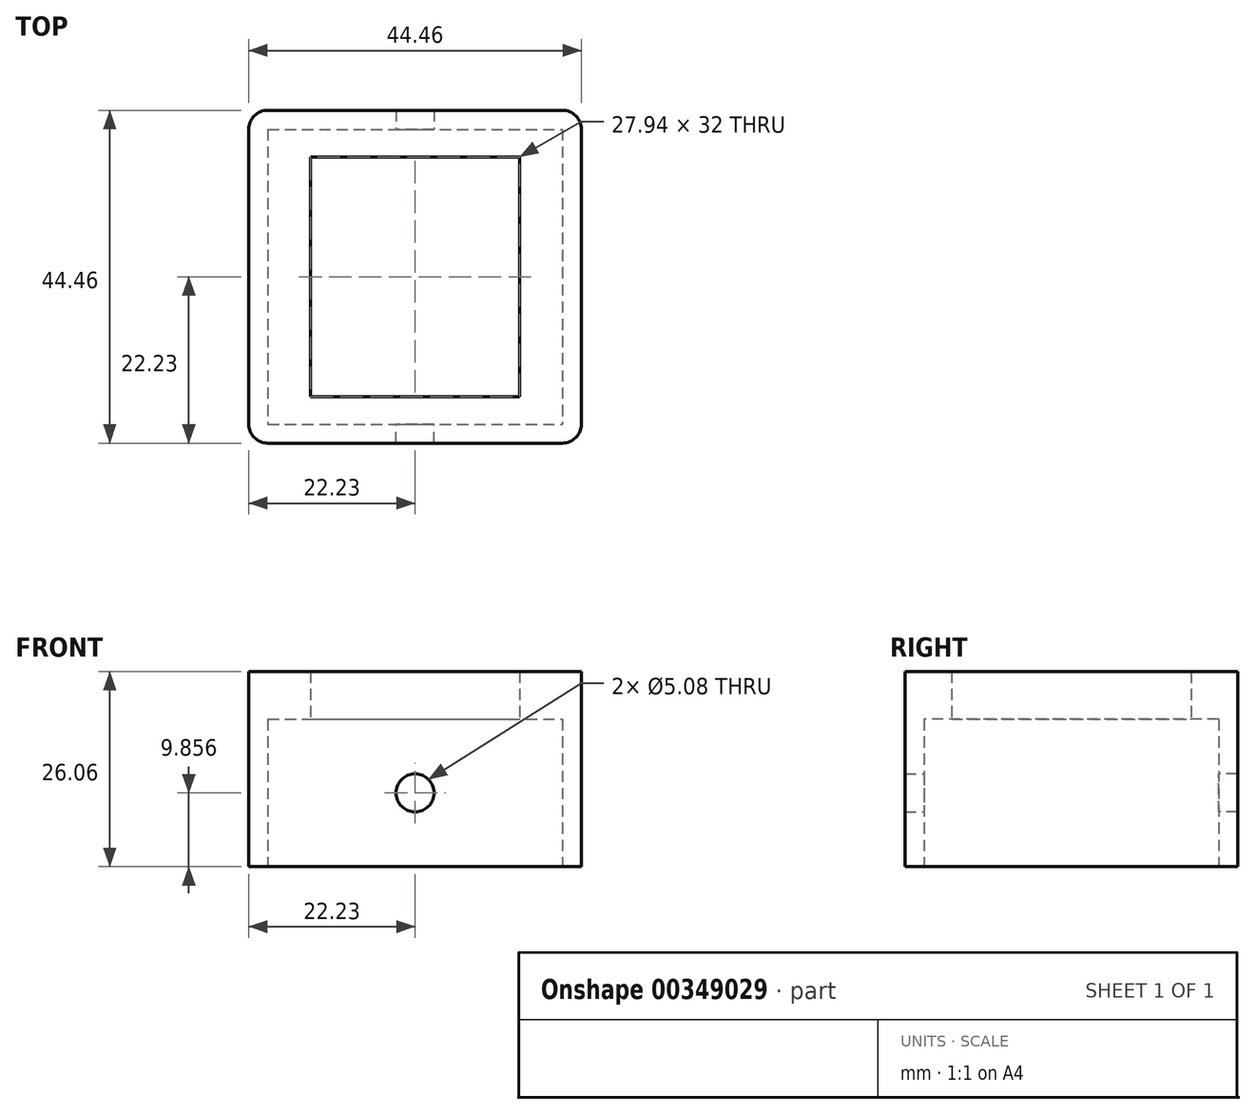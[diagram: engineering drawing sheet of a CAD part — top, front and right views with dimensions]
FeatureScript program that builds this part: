
annotation { "Feature Type Name" : "Feature", "Feature Type Description" : "" }
export const myFeature = defineFeature(function(context is Context, id is Id, definition is map)
    precondition{}
    {
        {
            var Q0;
            Q0=qCreatedBy(makeId("Top.planeOp"),FACE);
            var sketch = newSketch(context, id + "F0", { "sketchPlane" : qUnion([Q0])});
            skLineSegment(sketch, "E0.bottom", {"start": v(19.68, 19.69) * mm, "end": v(-19.69, 19.69) * mm});
            skLineSegment(sketch, "E0.top", {"start": v(19.69, -19.69) * mm, "end": v(-19.68, -19.69) * mm});
            skLineSegment(sketch, "E0.left", {"start": v(19.68, 19.69) * mm, "end": v(19.69, -19.69) * mm});
            skLineSegment(sketch, "E0.right", {"start": v(-19.69, 19.69) * mm, "end": v(-19.68, -19.69) * mm});
            skPoint(sketch, "E0.middle", {"position": v(0, 0) * mm});
            skLineSegment(sketch, "E1.0", {"start": v(19.69, -22.23) * mm, "end": v(-19.68, -22.23) * mm});
            skLineSegment(sketch, "E2.0", {"start": v(22.23, 19.69) * mm, "end": v(22.23, -19.69) * mm});
            skLineSegment(sketch, "E3.0", {"start": v(-22.23, 19.69) * mm, "end": v(-22.22, -19.69) * mm});
            skLineSegment(sketch, "E4.0", {"start": v(19.68, 22.23) * mm, "end": v(-19.69, 22.23) * mm});
            skArc(sketch, "E5", {"start": v(-19.69, 22.23) * mm, "mid": v(-20.82, 21.96) * mm, "end": v(-21.72, 21.21) * mm});
            skArc(sketch, "E6", {"start": v(-22.23, 19.69) * mm, "mid": v(-21.93, 20.86) * mm, "end": v(-21.13, 21.77) * mm});
            skArc(sketch, "E7", {"start": v(22.22, 19.69) * mm, "mid": v(21.48, 21.48) * mm, "end": v(19.68, 22.23) * mm});
            skArc(sketch, "E8", {"start": v(19.69, -22.23) * mm, "mid": v(21.48, -21.48) * mm, "end": v(22.23, -19.69) * mm});
            skArc(sketch, "E9", {"start": v(-22.22, -19.69) * mm, "mid": v(-21.48, -21.48) * mm, "end": v(-19.68, -22.23) * mm});
            skSolve(sketch);
        }
        {
            var Q0;
            Q0=qSketchRegion(id+"F0",true);
            extrude(context, id + "F1", {"entities" : qUnion([Q0]), "depth" : 26.21 * mm});
        }
        {
            var Q0;
            Q0=makeQuery(id+"F1.opExtrude","SWEPT_FACE",FACE,{"disambiguationData":[OSD([sQuery(id+"F0.wireOp",EDGE,"E0.top")])]});
            var sketch = newSketch(context, id + "F2", { "sketchPlane" : qUnion([Q0])});
            skLineSegment(sketch, "E10", {"start": v(-19.69, 26.21) * mm, "end": v(-19.69, 19.1) * mm});
            skLineSegment(sketch, "E11", {"start": v(19.68, 26.21) * mm, "end": v(19.68, 19.1) * mm});
            skLineSegment(sketch, "E12", {"start": v(19.68, 19.1) * mm, "end": v(-19.69, 19.1) * mm});
            skSolve(sketch);
        }
        {
            var Q0;
            Q0=makeQuery(id+"F2.imprint","IMPRINT",FACE,{"disambiguationData":[TD([[makeQuery(id+"F2.imprint","IMPRINT",EDGE,{"derivedFrom":sQuery(id+"F2.wireOp",EDGE,"E10")}),1.0]])]});
            extrude(context, id + "F3", {"entities" : qUnion([Q0]), "operationType" : NewBodyOperationType.ADD, "depth" : 40.3 * mm});
        }
        {
            var Q0;
            Q0=makeQuery(id+"F3.opExtrude","SWEPT_FACE",FACE,{"disambiguationData":[OSD([sQuery(id+"F2.wireOp",EDGE,"E12")])]});
            var sketch = newSketch(context, id + "F4", { "sketchPlane" : qUnion([Q0])});
            skPoint(sketch, "E13", {"position": v(0, 0) * mm});
            skLineSegment(sketch, "E14.bottom", {"start": v(-13.97, 16) * mm, "end": v(13.97, 16) * mm});
            skLineSegment(sketch, "E14.top", {"start": v(-13.97, -16) * mm, "end": v(13.97, -16) * mm});
            skLineSegment(sketch, "E14.left", {"start": v(-13.97, 16) * mm, "end": v(-13.97, -16) * mm});
            skLineSegment(sketch, "E14.right", {"start": v(13.97, 16) * mm, "end": v(13.97, -16) * mm});
            skSolve(sketch);
        }
        {
            var Q0;
            Q0=makeQuery(id+"F4.imprint","IMPRINT",FACE,{"disambiguationData":[TD([[makeQuery(id+"F4.imprint","IMPRINT",EDGE,{"derivedFrom":sQuery(id+"F4.wireOp",EDGE,"E14.bottom")}),-1.0]])]});
            extrude(context, id + "F5", {"entities" : qUnion([Q0]), "operationType" : NewBodyOperationType.REMOVE, "oppositeDirection" : true, "depth" : 25.4 * mm});
        }
        {
            var Q0;
            {var subQ0=sQuery(id+"F0.wireOp",EDGE,"E0.top");Q0=makeQuery(id+"F3.boolean.opBoolean","MERGE",FACE,{"derivedFrom":[makeQuery(id+"F1.opExtrude","CAP_FACE",FACE,{"disambiguationData":[OSD([sQuery(id+"F0.wireOp",EDGE,"E0.bottom"),subQ0,sQuery(id+"F0.wireOp",EDGE,"E0.left"),sQuery(id+"F0.wireOp",EDGE,"E0.right"),sQuery(id+"F0.wireOp",EDGE,"E1.0"),sQuery(id+"F0.wireOp",EDGE,"E2.0"),sQuery(id+"F0.wireOp",EDGE,"E3.0"),sQuery(id+"F0.wireOp",EDGE,"E4.0"),sQuery(id+"F0.wireOp",EDGE,"E5"),sQuery(id+"F0.wireOp",EDGE,"E6"),sQuery(id+"F0.wireOp",EDGE,"E7"),sQuery(id+"F0.wireOp",EDGE,"E8"),sQuery(id+"F0.wireOp",EDGE,"E9")])],"isStart":false}),makeQuery(id+"F3.opExtrude","SWEPT_FACE",FACE,{"disambiguationData":[OSD([subQ0])]})]});}
            extrude(context, id + "F6", {"entities" : qUnion([Q0]), "operationType" : NewBodyOperationType.REMOVE, "oppositeDirection" : true, "depth" : 0.76 * mm});
        }
        {
            var Q0;
            Q0=makeQuery(id+"F1.opExtrude","CAP_FACE",FACE,{"disambiguationData":[OSD([sQuery(id+"F0.wireOp",EDGE,"E0.bottom"),sQuery(id+"F0.wireOp",EDGE,"E0.top"),sQuery(id+"F0.wireOp",EDGE,"E0.left"),sQuery(id+"F0.wireOp",EDGE,"E0.right"),sQuery(id+"F0.wireOp",EDGE,"E1.0"),sQuery(id+"F0.wireOp",EDGE,"E2.0"),sQuery(id+"F0.wireOp",EDGE,"E3.0"),sQuery(id+"F0.wireOp",EDGE,"E4.0"),sQuery(id+"F0.wireOp",EDGE,"E5"),sQuery(id+"F0.wireOp",EDGE,"E6"),sQuery(id+"F0.wireOp",EDGE,"E7"),sQuery(id+"F0.wireOp",EDGE,"E8"),sQuery(id+"F0.wireOp",EDGE,"E9")])],"isStart":true});
            extrude(context, id + "F7", {"entities" : qUnion([Q0]), "operationType" : NewBodyOperationType.ADD, "depth" : 0.6 * mm});
        }
        {
            var Q0;
            {var subQ0=sQuery(id+"F0.wireOp",EDGE,"E0.top");Q0=makeQuery(id+"F7.boolean.opBoolean","MERGE",FACE,{"derivedFrom":[makeQuery(id+"F1.opExtrude","SWEPT_FACE",FACE,{"disambiguationData":[OSD([subQ0])]}),makeQuery(id+"F7.opExtrude","SWEPT_FACE",FACE,{"disambiguationData":[OSD([subQ0])]})]});}
            var sketch = newSketch(context, id + "F8", { "sketchPlane" : qUnion([Q0])});
            skLineSegment(sketch, "E15", {"start": v(0, -0.6) * mm, "end": v(0, 19.1) * mm});
            skPoint(sketch, "E16", {"position": v(0, 9.25) * mm});
            skCircle(sketch, "E17", {"center": v(0, 9.25) * mm, "radius": 2.54 * mm});
            skSolve(sketch);
        }
        {
            var Q0;
            Q0=qSketchRegion(id+"F8",true);
            extrude(context, id + "F9", {"entities" : qUnion([Q0]), "operationType" : NewBodyOperationType.REMOVE, "oppositeDirection" : true, "depth" : 7.62 * mm});
        }
        {
            var Q0;
            {var subQ0=sQuery(id+"F0.wireOp",EDGE,"E0.bottom");Q0=makeQuery(id+"F7.boolean.opBoolean","MERGE",FACE,{"derivedFrom":[makeQuery(id+"F1.opExtrude","SWEPT_FACE",FACE,{"disambiguationData":[OSD([subQ0])]}),makeQuery(id+"F7.opExtrude","SWEPT_FACE",FACE,{"disambiguationData":[OSD([subQ0])]})]});}
            var sketch = newSketch(context, id + "F10", { "sketchPlane" : qUnion([Q0])});
            skLineSegment(sketch, "E18", {"start": v(0, -0.6) * mm, "end": v(0, 19.1) * mm});
            skPoint(sketch, "E19", {"position": v(0, 9.25) * mm});
            skCircle(sketch, "E20", {"center": v(0, 9.25) * mm, "radius": 2.54 * mm});
            skSolve(sketch);
        }
        {
            var Q0;
            Q0=qSketchRegion(id+"F10",true);
            extrude(context, id + "F11", {"entities" : qUnion([Q0]), "operationType" : NewBodyOperationType.REMOVE, "oppositeDirection" : true, "depth" : 7.62 * mm});
        }
    });
